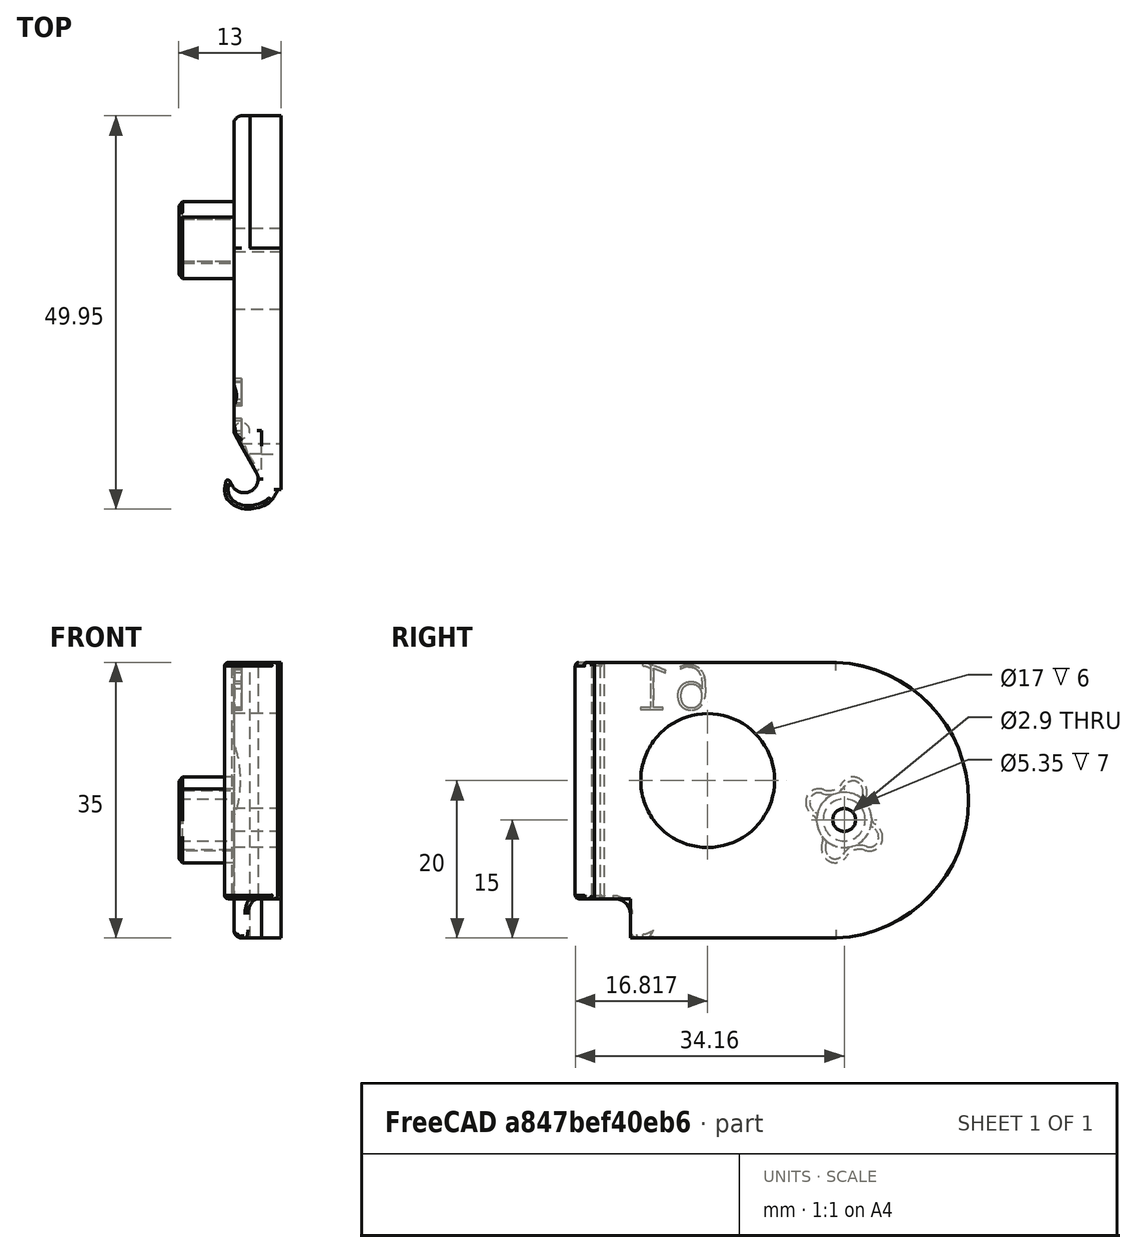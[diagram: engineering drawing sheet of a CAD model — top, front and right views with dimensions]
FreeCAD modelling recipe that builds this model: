
FCSTD DOCUMENT  (FreeCAD 0.18R)
Label: hinge-left-161deg-flat
License: All rights reserved
LicenseURL: http://en.wikipedia.org/wiki/All_rights_reserved
objects: App::FeaturePython×4, Part::FeaturePython×2, Part::Part2DObjectPython×1, Part::Extrusion×1, Part::Cut×1
note: 5 computed .brp shape members not serialized (recipe doc carries the construction recipe); baked Part::Feature solids carry a one-line shape summary decoded from their .brp

FEATURE [Part::FeaturePython] pillar_base_001  label="pillar-base_001"  # a2plus imported part (geometry in sourceFile) (typed FeaturePython)
  Placement = pos=(0.000608724,-1.42015,2.94708) rot=(-1,0,0;0.104894rad)
  a2p_Version = V0.1
  fixedPosition = false
  objectType = a2pPart
  sourceFile = ./parts/pillar-base.fcstd
  subassemblyImport = false
  timeLastImport = 1.60452e+09
  updateColors = true
FEATURE [Part::Part2DObjectPython] ShapeString  # Draft 2D object (typed FeaturePython)
  FontFile = <path>
  Placement = pos=(1.61,10.5,29) rot=(0.57735,-0.57735,-0.57735;2.0944rad)
  Size = 6
  String = 61
  Tracking = 0
FEATURE [Part::Extrusion] Extrude
  Base = -> ShapeString
  Dir = (-1,0,0)
  DirMode = 2
  FaceMakerClass = Part::FaceMakerBullseye
  LengthFwd = 2
  LengthRev = 0
  Solid = false
  Symmetric = false
FEATURE [Part::FeaturePython] bracket_left_flat_001  label="bracket-left-flat_001"  # a2plus imported part (geometry in sourceFile) (typed FeaturePython)
  a2p_Version = V0.1
  fixedPosition = true
  objectType = a2pPart
  sourceFile = ./parts/bracket-left-flat.fcstd
  subassemblyImport = false
  timeLastImport = 1.60454e+09
  updateColors = true
FEATURE [App::FeaturePython] axisCoincident_001  label="axisCoincident_001__bracket-left-flat_001"  # a2plus constraint (typed FeaturePython)
  Object1 = pillar_base_001
  Object2 = bracket_left_flat_001
  ParentTreeObject = -> pillar_base_001
  SubElement1 = Face17
  SubElement2 = Face48
  Suppressed = false
  Type = axial
  directionConstraint = 1
  lockRotation = false
FEATURE [App::FeaturePython] axisCoincident_001_mirror  label="axisCoincident_001__pillar-base_001"  # a2plus constraint (typed FeaturePython)
  Object1 = pillar_base_001
  Object2 = bracket_left_flat_001
  ParentTreeObject = -> bracket_left_flat_001
  SubElement1 = Face17
  SubElement2 = Face48
  Suppressed = false
  Type = axial
  directionConstraint = 1
  lockRotation = false
FEATURE [App::FeaturePython] planeCoincident_001  label="planeCoincident_001__bracket-left-flat_001"  # a2plus constraint (typed FeaturePython)
  Object1 = pillar_base_001
  Object2 = bracket_left_flat_001
  ParentTreeObject = -> pillar_base_001
  SubElement1 = Face1
  SubElement2 = Face72
  Suppressed = false
  Type = plane
  directionConstraint = 0
  offset = 0
FEATURE [App::FeaturePython] planeCoincident_001_mirror  label="planeCoincident_001__pillar-base_001"  # a2plus constraint (typed FeaturePython)
  Object1 = pillar_base_001
  Object2 = bracket_left_flat_001
  ParentTreeObject = -> bracket_left_flat_001
  SubElement1 = Face1
  SubElement2 = Face72
  Suppressed = false
  Type = plane
  directionConstraint = 0
  offset = 0
FEATURE [Part::Cut] Cut
  Base = -> bracket_left_flat_001
  Tool = -> Extrude
note: 1 file-system path scrubbed to <path> (originals preserved in the JSON sidecar)
